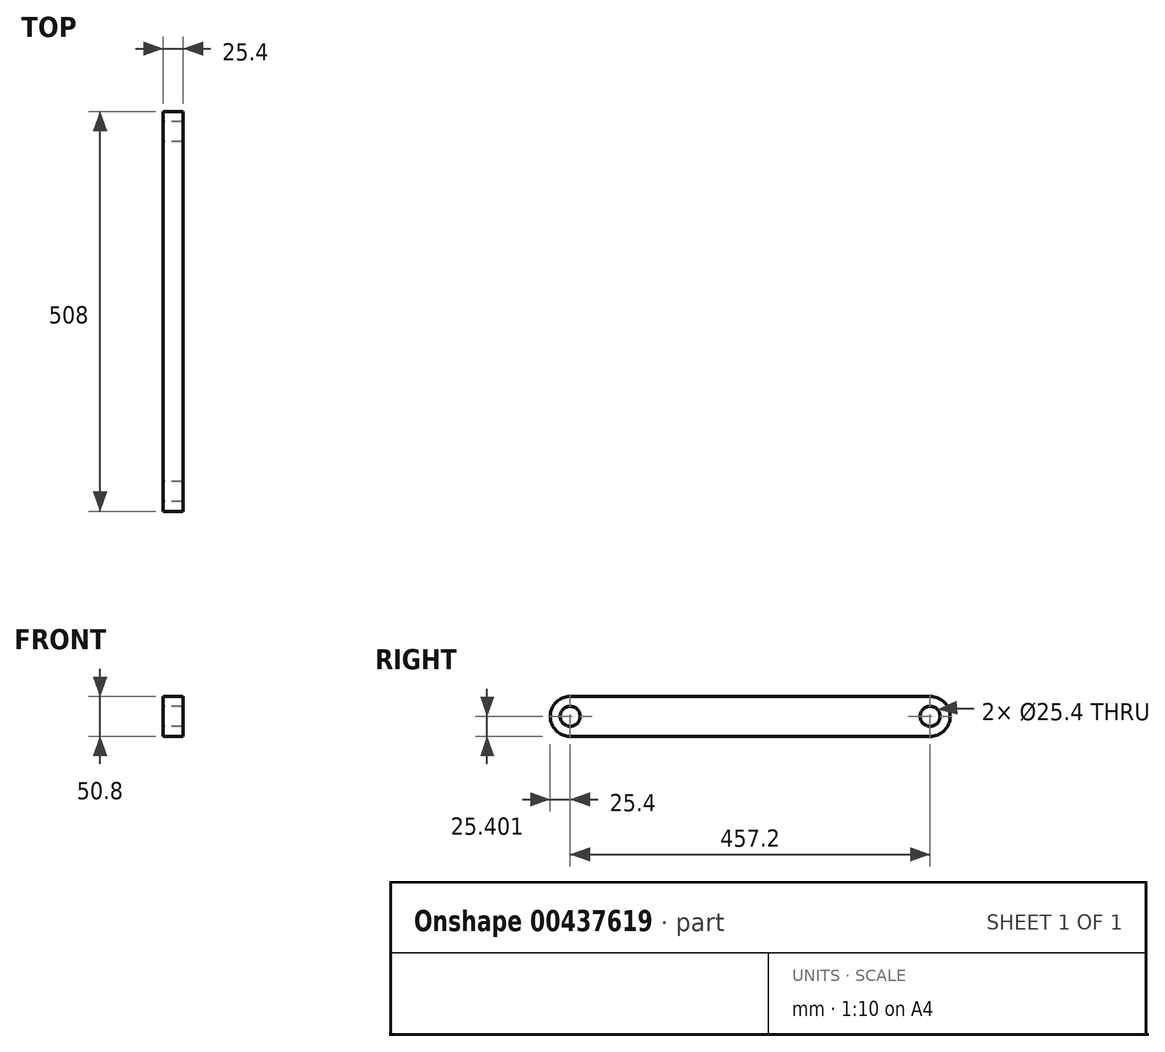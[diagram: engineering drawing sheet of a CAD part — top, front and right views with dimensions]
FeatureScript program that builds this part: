
annotation { "Feature Type Name" : "Feature", "Feature Type Description" : "" }
export const myFeature = defineFeature(function(context is Context, id is Id, definition is map)
    precondition{}
    {
        {
            var Q0;
            Q0=qCreatedBy(makeId("Right.planeOp"),FACE);
            var sketch = newSketch(context, id + "F0", { "sketchPlane" : qUnion([Q0])});
            skLineSegment(sketch, "E0.bottom", {"start": v(-63.06, 20.65) * mm, "end": v(394.14, 20.65) * mm});
            skLineSegment(sketch, "E0.top", {"start": v(-63.06, -30.15) * mm, "end": v(394.14, -30.15) * mm});
            skLineSegment(sketch, "E0.left", {"start": v(-63.06, 20.65) * mm, "end": v(-63.06, -30.15) * mm});
            skLineSegment(sketch, "E0.right", {"start": v(394.14, 20.65) * mm, "end": v(394.14, -30.15) * mm});
            skCircle(sketch, "E1", {"center": v(-63.06, -4.75) * mm, "radius": 25.4 * mm});
            skCircle(sketch, "E2", {"center": v(-63.06, -4.75) * mm, "radius": 12.7 * mm});
            skCircle(sketch, "E3", {"center": v(394.14, -4.75) * mm, "radius": 25.4 * mm});
            skCircle(sketch, "E4", {"center": v(394.14, -4.75) * mm, "radius": 12.7 * mm});
            skSolve(sketch);
        }
        {
            var Q0;
            Q0 = qSketchRegion(id + "F0", true);
            extrude(context, id + "F1", {"entities" : qUnion([Q0]), "depth" : 25.4 * mm});
        }
    });
